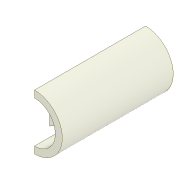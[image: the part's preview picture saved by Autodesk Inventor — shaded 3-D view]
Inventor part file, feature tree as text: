
AUTODESK INVENTOR PART (.ipt)
format: ipt  version: 2022 (Build 260153000, 153)  size: 180,224 bytes
history: native  units: mm
features: sketch x6, thicken_offset x5, extrude x3, hole x3, chamfer x1
ambient origin geometry x8: Origin, YZ Plane, XZ Plane, XY Plane, X Axis, Y Axis, Z Axis, Center Point
bodies: Solid1 (feature_tree)
feature tree (18):
  extrude  "Adapter"  Depth=9.0mm TaperAngle=0.0deg
  hole  "Hole1"  [1 undecoded]
  hole  "Hole2"  [1 undecoded]
  extrude  "Driver Gear Profile"  Depth=0.13mm
  extrude  "Motor Shaft Profile"  Depth=6.0mm
  chamfer  "Chamfer1"  Distance=5.5mm
  thicken_offset  "Thicken1"
  thicken_offset  "Thicken2"
  thicken_offset  "Thicken3"
  thicken_offset  "Thicken5"
  thicken_offset  "Thicken6"
  hole  "Hole6"  [1 undecoded]
  sketch  "Sketch1"  dims[d1=11.0mm d2=9.0mm d3=0.0mm]
  sketch  "Sketch2"  dims[d4=13.0mm d5=0.0mm]
  sketch  "Sketch3"  dims[d6=8.0mm d7=6.0mm d8=4.0mm d9=2.0mm d10=90.0deg d11=5.0mm d12=0.0mm]
  sketch  "Sketch4"  dims[d13=6.3mm d14=6.0mm d15=4.0mm d16=2.0mm d17=90.0deg d18=4.0mm d19=0.0mm d20=4.0mm]
  sketch  "Sketch6"  dims[d21=6.0mm d22=0.0mm d27=0.1mm d28=0.15mm]
  sketch  "Sketch9"  dims[d29=0.15mm d30=0.15mm d31=0.13mm d32=0.15mm d35=6.0mm d36=5.5mm d37=12.0mm d38=0.0mm d39=0.2mm d40=0.1mm d48=0.5mm d49=2.0mm d50=45.0deg d58=0.2mm d59=0.2mm d67=2.85mm d68=7.0mm d69=4.0mm d70=2.0mm d71=90.0deg d72=10.4mm d73=20.594885mm d41=1.0mm d42=1.0mm d43=1.0mm d44=0.15mm d45=0.25mm d46=0.375mm d47=14.3117mm d51=0.75mm d52=0.375mm d60=0.5mm d61=0.872665mm]
note: 3 required parameter values undecoded (feature->parameter linkage not recoverable at this tier; creation-order binding heuristic only, values carry confidence <= 0.55)
